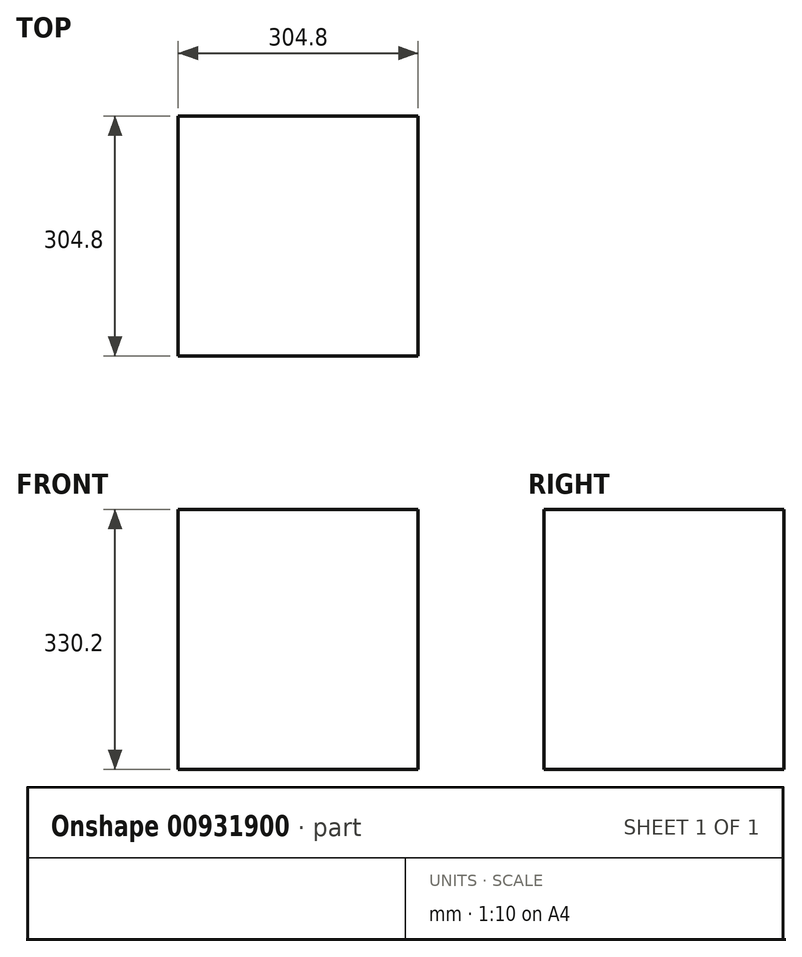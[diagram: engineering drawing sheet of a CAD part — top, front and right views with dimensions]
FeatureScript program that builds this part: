
annotation { "Feature Type Name" : "Feature", "Feature Type Description" : "" }
export const myFeature = defineFeature(function(context is Context, id is Id, definition is map)
    precondition{}
    {
        {
            var Q0;
            Q0=qCreatedBy(makeId("Top.planeOp"),FACE);
            var sketch = newSketch(context, id + "F0", { "sketchPlane" : qUnion([Q0])});
            skLineSegment(sketch, "E0.bottom", {"start": v(0, 0) * mm, "end": v(304.8, 0) * mm});
            skLineSegment(sketch, "E0.top", {"start": v(0, -304.8) * mm, "end": v(304.8, -304.8) * mm});
            skLineSegment(sketch, "E0.left", {"start": v(0, 0) * mm, "end": v(0, -304.8) * mm});
            skLineSegment(sketch, "E0.right", {"start": v(304.8, 0) * mm, "end": v(304.8, -304.8) * mm});
            skSolve(sketch);
        }
        {
            var Q0;
            Q0 = qSketchRegion(id + "F0", true);
            extrude(context, id + "F1", {"entities" : qUnion([Q0]), "oppositeDirection" : true, "depth" : 330.2 * mm, "offsetDistance" : 25.4 * mm});
        }
    });
